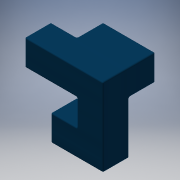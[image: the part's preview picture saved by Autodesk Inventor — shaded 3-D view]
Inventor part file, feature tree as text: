
AUTODESK INVENTOR PART (.ipt)
format: ipt  version: 2016 (Build 200138000, 138)  size: 169,472 bytes
history: native  units: in
note: dims shown in document units (in); Inventor stores cm internally (conversion verified against a paired STEP export)
features: plane x8, extrude x2, other x1, fillet x1, sketch x1
ambient origin geometry x8: Origin, YZ Plane, XZ Plane, XY Plane, X Axis, Y Axis, Z Axis, Center Point
bodies: Solid1 (feature_tree)
feature tree (13):
  other  "Cube Master.ipt"
  extrude  "Extrusion1"  Depth=0.3937in
  extrude  "Extrusion2"  Depth=0.0193in TaperAngle=0.0deg
  fillet  "Fillet1"  Radius=1.0in
  sketch  "Sketch1"  dims[d0=0.3937in d1=0.3937in d2=1.0in d3=0.0in d4=1.0in d5=0.0in d7=0.0193in d8=0.0193in]
  plane  "Work Plane1"
  plane  "Work Plane2"
  plane  "Work Plane3"
  plane  "Work Plane4"
  plane  "Work Plane5"
  plane  "Work Plane6"
  plane  "Work Plane7"
  plane  "Work Plane8"
